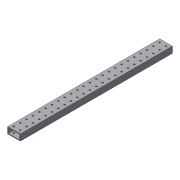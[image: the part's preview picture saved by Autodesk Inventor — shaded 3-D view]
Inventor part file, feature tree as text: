
AUTODESK INVENTOR PART (.ipt)
format: ipt  version: 2012 (Build 160160000, 160)  size: 163,840 bytes
history: native  units: in
note: dims shown in document units (in); Inventor stores cm internally (conversion verified against a paired STEP export)
features: extrude x2, sketch x2, shell x1, pattern_linear x1
ambient origin geometry x8: Origin, YZ Plane, XZ Plane, XY Plane, X Axis, Y Axis, Z Axis, Center Point
bodies: Solid1 (feature_tree)
feature tree (6):
  extrude  "Extrusion1"  Depth=2.0in
  shell  "Shell1"  Thickness=24.0in
  extrude  "Extrusion2"  Depth=0.5in
  pattern_linear  "Rectangular Pattern1"  Spacing1=0.5in  [1 undecoded]
  sketch  "Sketch1"  dims[d0=1.0in d1=2.0in d2=24.0in d3=0.0in]
  sketch  "Sketch2"  dims[d4=0.125in d5=0.5in d6=0.5in d7=0.25in d8=24.0in d9=0.0in d10=9.4488in d12=1.0in d13=0.7874in d15=1.0in]
note: 1 required parameter value undecoded (feature->parameter linkage not recoverable at this tier; creation-order binding heuristic only, values carry confidence <= 0.55)
